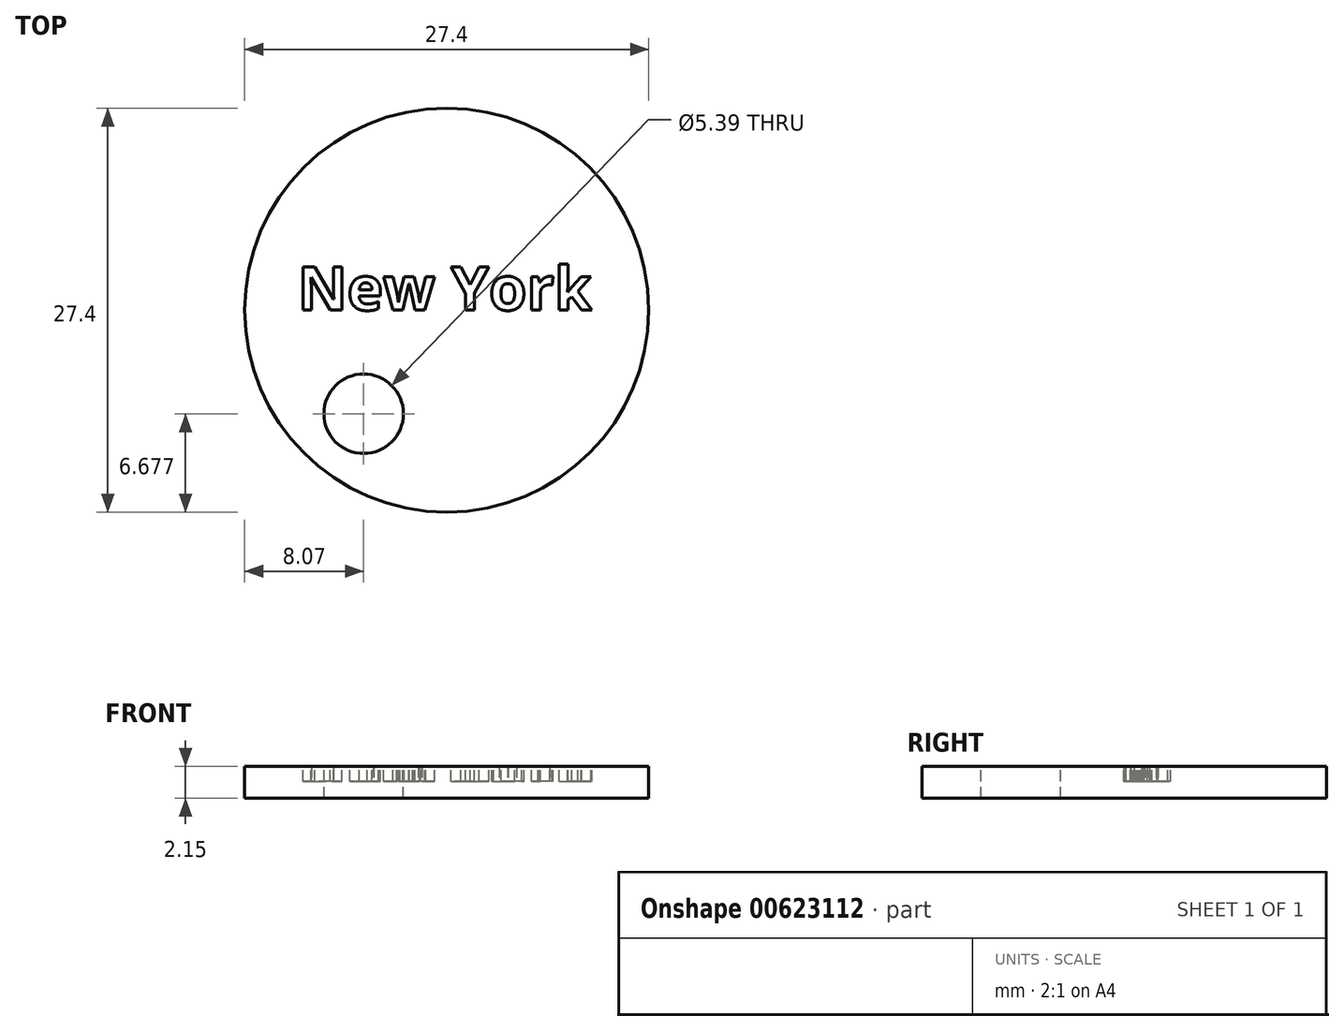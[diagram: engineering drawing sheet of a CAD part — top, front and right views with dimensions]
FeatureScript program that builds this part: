
annotation { "Feature Type Name" : "Feature", "Feature Type Description" : "" }
export const myFeature = defineFeature(function(context is Context, id is Id, definition is map)
    precondition{}
    {
        {
            var Q0;
            Q0=qCreatedBy(makeId("Top.planeOp"),FACE);
            var sketch = newSketch(context, id + "F0", { "sketchPlane" : qUnion([Q0])});
            skCircle(sketch, "E0", {"center": v(0, 0) * mm, "radius": 13.7 * mm});
            skSolve(sketch);
        }
        {
            var Q0;
            Q0=makeQuery(id+"F0.imprint","IMPRINT",FACE,{"disambiguationData":[TD([[makeQuery(id+"F0.imprint","IMPRINT",EDGE,{"derivedFrom":sQuery(id+"F0.wireOp",EDGE,"E0")}),1.0]])]});
            extrude(context, id + "F1", {"entities" : qUnion([Q0]), "depth" : 2.15 * mm, "offsetDistance" : 25 * mm});
        }
        {
            var Q0;
            Q0=makeQuery(id+"F1.opExtrude","CAP_FACE",FACE,{"disambiguationData":[OSD([sQuery(id+"F0.wireOp",EDGE,"E0")])],"isStart":false});
            var sketch = newSketch(context, id + "F2", { "sketchPlane" : qUnion([Q0])});
            skCircle(sketch, "E1", {"center": v(-5.63, -7.02) * mm, "radius": 2.7 * mm});
            skSolve(sketch);
        }
        {
            var Q0;
            Q0 = qSketchRegion(id + "F2", true);
            extrude(context, id + "F3", {"entities" : qUnion([Q0]), "operationType" : NewBodyOperationType.REMOVE, "oppositeDirection" : true, "depth" : 25 * mm, "offsetDistance" : 25 * mm});
        }
        {
            var Q0;
            Q0=makeQuery(id+"F1.opExtrude","CAP_FACE",FACE,{"disambiguationData":[OSD([sQuery(id+"F0.wireOp",EDGE,"E0")])],"isStart":false});
            var sketch = newSketch(context, id + "F4", { "sketchPlane" : qUnion([Q0])});
            skText(sketch, "E2", { "text": "New York", "fontName": "OpenSans-Bold.ttf"});
            const initialGuessF4  = {"E2": [-0.0101, 0, 1, 0, 0.00297]};
            skSetInitialGuess(sketch, initialGuessF4);
            skSolve(sketch);
        }
        {
            var Q0;
            Q0 = qSketchRegion(id + "F4", true);
            extrude(context, id + "F5", {"entities" : qUnion([Q0]), "operationType" : NewBodyOperationType.REMOVE, "oppositeDirection" : true, "depth" : 1 * mm, "offsetDistance" : 25 * mm});
        }
    });
